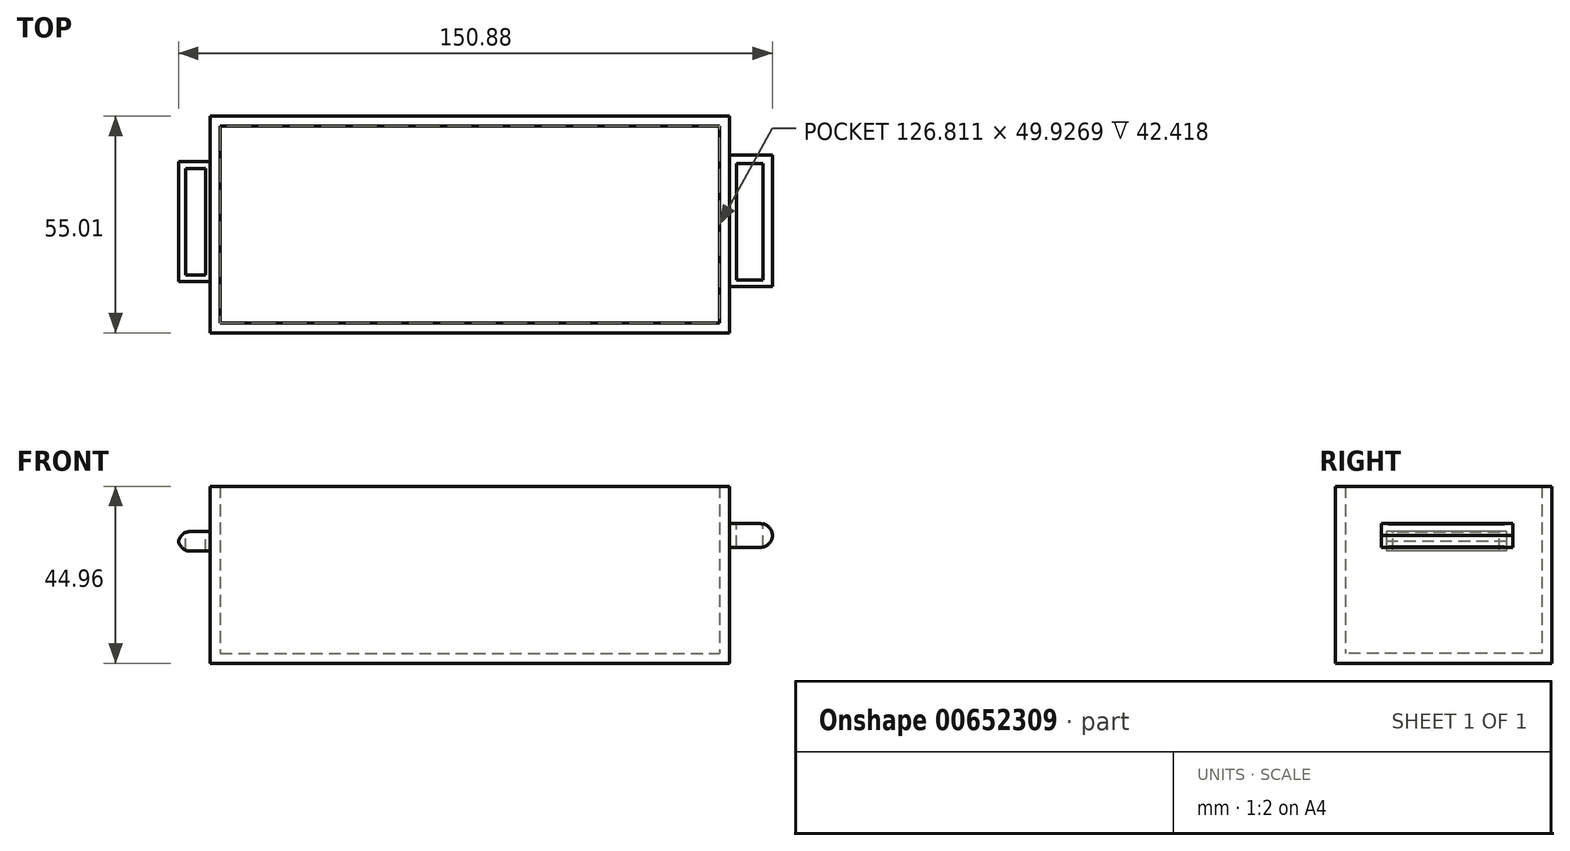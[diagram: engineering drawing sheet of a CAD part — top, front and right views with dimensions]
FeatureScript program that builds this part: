
annotation { "Feature Type Name" : "Feature", "Feature Type Description" : "" }
export const myFeature = defineFeature(function(context is Context, id is Id, definition is map)
    precondition{}
    {
        {
            var Q0;
            Q0=qCreatedBy(makeId("Top.planeOp"),FACE);
            var sketch = newSketch(context, id + "F0", { "sketchPlane" : qUnion([Q0])});
            skLineSegment(sketch, "E0.bottom", {"start": v(-65.79, 38.6) * mm, "end": v(66.1, 38.6) * mm});
            skLineSegment(sketch, "E0.top", {"start": v(-65.79, -16.4) * mm, "end": v(66.1, -16.4) * mm});
            skLineSegment(sketch, "E0.left", {"start": v(-65.79, 38.6) * mm, "end": v(-65.79, -16.4) * mm});
            skLineSegment(sketch, "E0.right", {"start": v(66.1, 38.6) * mm, "end": v(66.1, -16.4) * mm});
            skSolve(sketch);
        }
        {
            var Q0;
            Q0 = qSketchRegion(id + "F0", true);
            extrude(context, id + "F1", {"entities" : qUnion([Q0]), "depth" : 44.96 * mm, "offsetDistance" : 25.4 * mm});
        }
        {
            var Q0;
            Q0=makeQuery(id+"F1.opExtrude","CAP_FACE",FACE,{"disambiguationData":[OSD([sQuery(id+"F0.wireOp",EDGE,"E0.bottom"),sQuery(id+"F0.wireOp",EDGE,"E0.top"),sQuery(id+"F0.wireOp",EDGE,"E0.left"),sQuery(id+"F0.wireOp",EDGE,"E0.right")])],"isStart":false});
            shell(context, id + "F2", {"entities" : qUnion([Q0]), "thickness" : 2.54 * mm});
        }
        {
            var Q0;
            Q0=makeQuery(id+"F1.opExtrude","SWEPT_FACE",FACE,{"disambiguationData":[OSD([sQuery(id+"F0.wireOp",EDGE,"E0.right")])]});
            var sketch = newSketch(context, id + "F3", { "sketchPlane" : qUnion([Q0])});
            skLineSegment(sketch, "E1.bottom", {"start": v(-4.66, 35.46) * mm, "end": v(28.72, 35.46) * mm});
            skLineSegment(sketch, "E1.top", {"start": v(-4.66, 29.44) * mm, "end": v(28.72, 29.44) * mm});
            skLineSegment(sketch, "E1.left", {"start": v(-4.66, 35.46) * mm, "end": v(-4.66, 29.44) * mm});
            skLineSegment(sketch, "E1.right", {"start": v(28.72, 35.46) * mm, "end": v(28.72, 29.44) * mm});
            skSolve(sketch);
        }
        {
            var Q0;
            Q0 = qSketchRegion(id + "F3", true);
            extrude(context, id + "F4", {"entities" : qUnion([Q0]), "operationType" : NewBodyOperationType.ADD, "depth" : 10.92 * mm, "offsetDistance" : 25.4 * mm});
        }
        {
            var Q0;
            Q0=makeQuery(id+"F4.opExtrude","SWEPT_FACE",FACE,{"disambiguationData":[OSD([sQuery(id+"F3.wireOp",EDGE,"E1.bottom")])]});
            var sketch = newSketch(context, id + "F5", { "sketchPlane" : qUnion([Q0])});
            skLineSegment(sketch, "E2.bottom", {"start": v(67.88, -2.94) * mm, "end": v(74.6, -2.94) * mm});
            skLineSegment(sketch, "E2.top", {"start": v(67.88, 26.6) * mm, "end": v(74.6, 26.6) * mm});
            skLineSegment(sketch, "E2.left", {"start": v(67.88, -2.94) * mm, "end": v(67.88, 26.6) * mm});
            skLineSegment(sketch, "E2.right", {"start": v(74.6, -2.94) * mm, "end": v(74.6, 26.6) * mm});
            skSolve(sketch);
        }
        {
            var Q0;
            Q0 = qSketchRegion(id + "F5", true);
            extrude(context, id + "F6", {"entities" : qUnion([Q0]), "operationType" : NewBodyOperationType.REMOVE, "oppositeDirection" : true, "depth" : 25.4 * mm, "offsetDistance" : 25.4 * mm});
        }
        {
            var Q0;
            Q0=makeQuery(id+"F4.opExtrude","CAP_EDGE",EDGE,{"disambiguationData":[OSD([sQuery(id+"F3.wireOp",EDGE,"E1.bottom")])],"isStart":false});
            var Q1;
            Q1=makeQuery(id+"F4.opExtrude","CAP_EDGE",EDGE,{"disambiguationData":[OSD([sQuery(id+"F3.wireOp",EDGE,"E1.top")])],"isStart":false});
            fillet(context, id + "F7", {"entities" : qUnion([Q0, Q1]), "radius" : 3.07 * mm, "tangentPropagation" : true, "allowEdgeOverflow" : false});
        }
        {
            var Q0;
            Q0=makeQuery(id+"F1.opExtrude","SWEPT_FACE",FACE,{"disambiguationData":[OSD([sQuery(id+"F0.wireOp",EDGE,"E0.left")])]});
            var sketch = newSketch(context, id + "F8", { "sketchPlane" : qUnion([Q0])});
            skLineSegment(sketch, "E3.bottom", {"start": v(-27.1, 33.46) * mm, "end": v(3.36, 33.46) * mm});
            skLineSegment(sketch, "E3.top", {"start": v(-27.1, 28.48) * mm, "end": v(3.36, 28.48) * mm});
            skLineSegment(sketch, "E3.left", {"start": v(-27.1, 33.46) * mm, "end": v(-27.1, 28.48) * mm});
            skLineSegment(sketch, "E3.right", {"start": v(3.36, 33.46) * mm, "end": v(3.36, 28.48) * mm});
            skSolve(sketch);
        }
        {
            var Q0;
            Q0=makeQuery(id+"F8.imprint","IMPRINT",FACE,{"disambiguationData":[TD([[makeQuery(id+"F8.imprint","IMPRINT",EDGE,{"derivedFrom":sQuery(id+"F8.wireOp",EDGE,"E3.bottom")}),-1.0]])]});
            extrude(context, id + "F9", {"entities" : qUnion([Q0]), "operationType" : NewBodyOperationType.ADD, "depth" : 8.13 * mm, "offsetDistance" : 25.4 * mm});
        }
        {
            var Q0;
            Q0=makeQuery(id+"F9.opExtrude","SWEPT_FACE",FACE,{"disambiguationData":[OSD([sQuery(id+"F8.wireOp",EDGE,"E3.bottom")])]});
            var sketch = newSketch(context, id + "F10", { "sketchPlane" : qUnion([Q0])});
            skLineSegment(sketch, "E4.bottom", {"start": v(-72, 25.36) * mm, "end": v(-67, 25.36) * mm});
            skLineSegment(sketch, "E4.top", {"start": v(-72, -1.68) * mm, "end": v(-67, -1.68) * mm});
            skLineSegment(sketch, "E4.left", {"start": v(-72, 25.36) * mm, "end": v(-72, -1.68) * mm});
            skLineSegment(sketch, "E4.right", {"start": v(-67, 25.36) * mm, "end": v(-67, -1.68) * mm});
            skSolve(sketch);
        }
        {
            var Q0;
            Q0=makeQuery(id+"F10.imprint","IMPRINT",FACE,{"disambiguationData":[TD([[makeQuery(id+"F10.imprint","IMPRINT",EDGE,{"derivedFrom":sQuery(id+"F10.wireOp",EDGE,"E4.bottom")}),-1.0]])]});
            extrude(context, id + "F11", {"entities" : qUnion([Q0]), "operationType" : NewBodyOperationType.REMOVE, "oppositeDirection" : true, "depth" : 25.4 * mm, "offsetDistance" : 25.4 * mm});
        }
        {
            var Q0;
            Q0=makeQuery(id+"F9.opExtrude","CAP_EDGE",EDGE,{"disambiguationData":[OSD([sQuery(id+"F8.wireOp",EDGE,"E3.bottom")])],"isStart":false});
            var Q1;
            Q1=makeQuery(id+"F9.opExtrude","CAP_EDGE",EDGE,{"disambiguationData":[OSD([sQuery(id+"F8.wireOp",EDGE,"E3.top")])],"isStart":false});
            fillet(context, id + "F12", {"entities" : qUnion([Q0, Q1]), "radius" : 3.07 * mm, "tangentPropagation" : true, "allowEdgeOverflow" : false});
        }
    });
